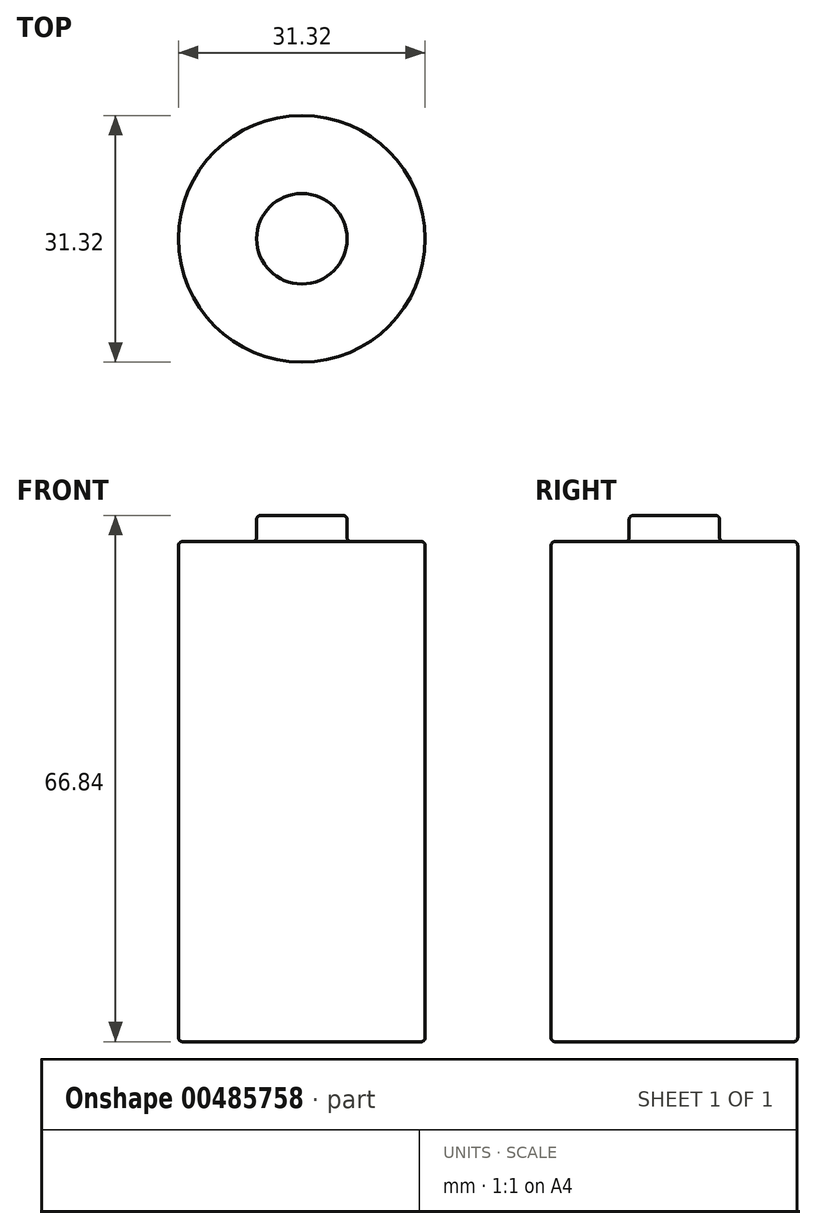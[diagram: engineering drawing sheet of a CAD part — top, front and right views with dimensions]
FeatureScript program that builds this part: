
annotation { "Feature Type Name" : "Feature", "Feature Type Description" : "" }
export const myFeature = defineFeature(function(context is Context, id is Id, definition is map)
    precondition{}
    {
        {
            var Q0;
            Q0=qCreatedBy(makeId("Front.planeOp"),FACE);
            var sketch = newSketch(context, id + "F0", { "sketchPlane" : qUnion([Q0])});
            skLineSegment(sketch, "E0.bottom", {"start": v(0, 0) * mm, "end": v(-15.66, 0) * mm});
            skLineSegment(sketch, "E0.top", {"start": v(0, 63.53) * mm, "end": v(-15.66, 63.53) * mm});
            skLineSegment(sketch, "E0.left", {"start": v(0, 0) * mm, "end": v(0, 63.53) * mm});
            skLineSegment(sketch, "E0.right", {"start": v(-15.66, 0) * mm, "end": v(-15.66, 63.53) * mm});
            skLineSegment(sketch, "E1.bottom", {"start": v(0, 63.53) * mm, "end": v(-5.75, 63.53) * mm});
            skLineSegment(sketch, "E1.top", {"start": v(0, 66.84) * mm, "end": v(-5.75, 66.84) * mm});
            skLineSegment(sketch, "E1.left", {"start": v(0, 63.53) * mm, "end": v(0, 66.84) * mm});
            skLineSegment(sketch, "E1.right", {"start": v(-5.75, 63.53) * mm, "end": v(-5.75, 66.84) * mm});
            skSolve(sketch);
        }
        {
            var Q0;
            Q0 = qSketchRegion(id + "F0", true);
            var Q1;
            Q1=sQuery(id+"F0.wireOp",EDGE,"E0.left");
            revolve(context, id + "F1", {"entities" : qUnion([Q0]), "axis" : qUnion([Q1]), "revolveType" : RevolveType.FULL});
        }
        {
            var Q0;
            Q0=makeQuery(id+"F1.opRevolve","SWEPT_EDGE",EDGE,{"disambiguationData":[OSD([sQuery(id+"F0.wireOp",EDGE,"E1.top"),sQuery(id+"F0.wireOp",EDGE,"E1.right")])]});
            var Q1;
            Q1=makeQuery(id+"F1.opRevolve","SWEPT_EDGE",EDGE,{"disambiguationData":[OSD([sQuery(id+"F0.wireOp",EDGE,"E0.top"),sQuery(id+"F0.wireOp",EDGE,"E1.bottom"),sQuery(id+"F0.wireOp",EDGE,"E1.right")])]});
            var Q2;
            Q2=makeQuery(id+"F1.opRevolve","SWEPT_EDGE",EDGE,{"disambiguationData":[OSD([sQuery(id+"F0.wireOp",EDGE,"E0.top"),sQuery(id+"F0.wireOp",EDGE,"E0.right")])]});
            var Q3;
            Q3=makeQuery(id+"F1.opRevolve","SWEPT_EDGE",EDGE,{"disambiguationData":[OSD([sQuery(id+"F0.wireOp",EDGE,"E0.bottom"),sQuery(id+"F0.wireOp",EDGE,"E0.right")])]});
            fillet(context, id + "F2", {"entities" : qUnion([Q0, Q1, Q2, Q3]), "radius" : 0.5 * mm, "tangentPropagation" : true, "allowEdgeOverflow" : false});
        }
    });
